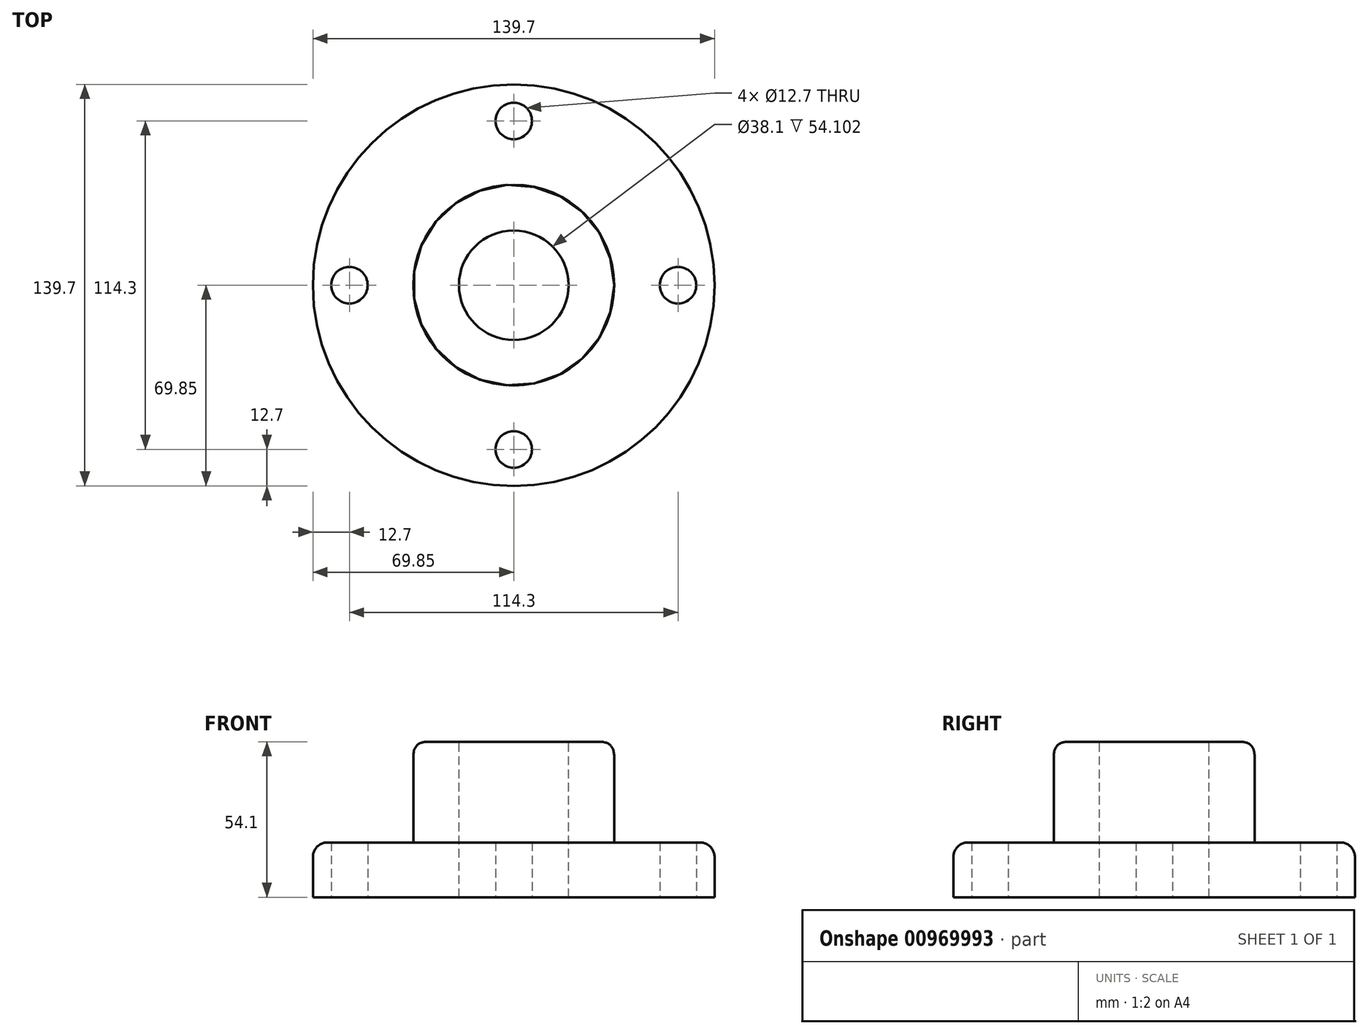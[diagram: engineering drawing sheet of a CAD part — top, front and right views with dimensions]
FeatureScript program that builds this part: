
annotation { "Feature Type Name" : "Feature", "Feature Type Description" : "" }
export const myFeature = defineFeature(function(context is Context, id is Id, definition is map)
    precondition{}
    {
        {
            var Q0;
            Q0=qCreatedBy(makeId("Top.planeOp"),FACE);
            var sketch = newSketch(context, id + "F0", { "sketchPlane" : qUnion([Q0])});
            skCircle(sketch, "E0", {"center": v(0, 0) * mm, "radius": 69.85 * mm});
            skSolve(sketch);
        }
        {
            var Q0;
            Q0=makeQuery(id+"F0.imprint","IMPRINT",FACE,{"disambiguationData":[TD([[makeQuery(id+"F0.imprint","IMPRINT",EDGE,{"derivedFrom":sQuery(id+"F0.wireOp",EDGE,"E0")}),1.0]])]});
            extrude(context, id + "F1", {"entities" : qUnion([Q0]), "depth" : 19.05 * mm, "offsetDistance" : 25.4 * mm});
        }
        {
            var Q0;
            Q0=qCreatedBy(makeId("Top.planeOp"),FACE);
            var sketch = newSketch(context, id + "F2", { "sketchPlane" : qUnion([Q0])});
            skCircle(sketch, "E1", {"center": v(-57.15, 0) * mm, "radius": 6.35 * mm});
            skCircle(sketch, "E2", {"center": v(57.15, 0) * mm, "radius": 6.35 * mm});
            skCircle(sketch, "E3", {"center": v(0, 57.15) * mm, "radius": 6.35 * mm});
            skCircle(sketch, "E4", {"center": v(0, -57.15) * mm, "radius": 6.35 * mm});
            skSolve(sketch);
        }
        {
            var Q0;
            Q0=makeQuery(id+"F2.imprint","IMPRINT",FACE,{"disambiguationData":[TD([[makeQuery(id+"F2.imprint","IMPRINT",EDGE,{"derivedFrom":sQuery(id+"F2.wireOp",EDGE,"E2")}),1.0]])]});
            var Q1;
            Q1=makeQuery(id+"F2.imprint","IMPRINT",FACE,{"disambiguationData":[TD([[makeQuery(id+"F2.imprint","IMPRINT",EDGE,{"derivedFrom":sQuery(id+"F2.wireOp",EDGE,"E3")}),1.0]])]});
            var Q2;
            Q2=makeQuery(id+"F2.imprint","IMPRINT",FACE,{"disambiguationData":[TD([[makeQuery(id+"F2.imprint","IMPRINT",EDGE,{"derivedFrom":sQuery(id+"F2.wireOp",EDGE,"E1")}),1.0]])]});
            var Q3;
            Q3=makeQuery(id+"F2.imprint","IMPRINT",FACE,{"disambiguationData":[TD([[makeQuery(id+"F2.imprint","IMPRINT",EDGE,{"derivedFrom":sQuery(id+"F2.wireOp",EDGE,"E4")}),1.0]])]});
            extrude(context, id + "F3", {"entities" : qUnion([Q0, Q1, Q2, Q3]), "operationType" : NewBodyOperationType.REMOVE, "depth" : 25.4 * mm, "offsetDistance" : 25.4 * mm});
        }
        {
            var Q0;
            Q0=makeQuery(id+"F1.opExtrude","CAP_EDGE",EDGE,{"disambiguationData":[OSD([sQuery(id+"F0.wireOp",EDGE,"E0")])],"isStart":false});
            fillet(context, id + "F4", {"entities" : qUnion([Q0]), "radius" : 5.08 * mm, "tangentPropagation" : true, "allowEdgeOverflow" : false});
        }
        {
            var Q0;
            Q0=makeQuery(id+"F1.opExtrude","CAP_FACE",FACE,{"disambiguationData":[OSD([sQuery(id+"F0.wireOp",EDGE,"E0")])],"isStart":false});
            var sketch = newSketch(context, id + "F5", { "sketchPlane" : qUnion([Q0])});
            skCircle(sketch, "E5", {"center": v(0, 0) * mm, "radius": 34.93 * mm});
            skSolve(sketch);
        }
        {
            var Q0;
            Q0 = qSketchRegion(id + "F5", true);
            extrude(context, id + "F6", {"entities" : qUnion([Q0]), "operationType" : NewBodyOperationType.ADD, "depth" : 35.05 * mm, "offsetDistance" : 25.4 * mm});
        }
        {
            var Q0;
            Q0=makeQuery(id+"F6.opExtrude","CAP_EDGE",EDGE,{"disambiguationData":[OSD([sQuery(id+"F5.wireOp",EDGE,"E5")])],"isStart":true});
            var Q1;
            Q1=makeQuery(id+"F6.opExtrude","CAP_EDGE",EDGE,{"disambiguationData":[OSD([sQuery(id+"F5.wireOp",EDGE,"E5")])],"isStart":false});
            fillet(context, id + "F7", {"entities" : qUnion([Q0, Q1]), "radius" : 5.08 * mm, "rho" : 0.5, "crossSection" : FilletCrossSection.CONIC, "allowEdgeOverflow" : false});
        }
        {
            var Q0;
            Q0=makeQuery(id+"F6.opExtrude","CAP_FACE",FACE,{"disambiguationData":[OSD([sQuery(id+"F5.wireOp",EDGE,"E5")])],"isStart":false});
            var sketch = newSketch(context, id + "F8", { "sketchPlane" : qUnion([Q0])});
            skCircle(sketch, "E6", {"center": v(0, 0) * mm, "radius": 19.05 * mm});
            skSolve(sketch);
        }
        {
            var Q0;
            Q0 = qSketchRegion(id + "F8", true);
            extrude(context, id + "F9", {"entities" : qUnion([Q0]), "operationType" : NewBodyOperationType.REMOVE, "oppositeDirection" : true, "depth" : 76.2 * mm, "offsetDistance" : 25.4 * mm});
        }
    });
